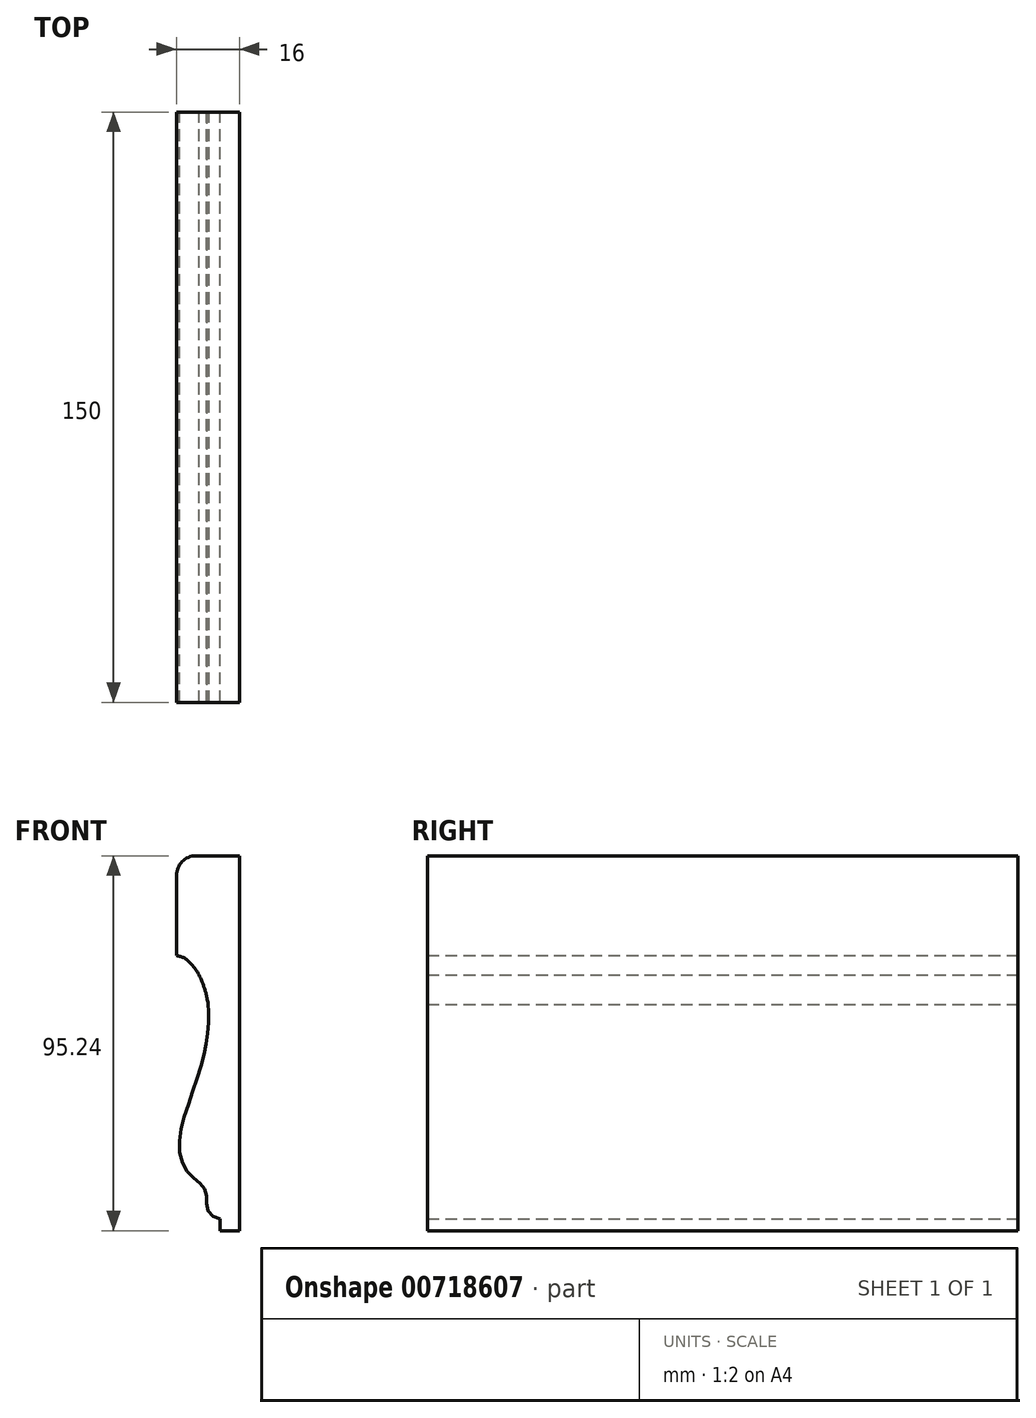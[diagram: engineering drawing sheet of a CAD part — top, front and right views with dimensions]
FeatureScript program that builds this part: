
annotation { "Feature Type Name" : "Feature", "Feature Type Description" : "" }
export const myFeature = defineFeature(function(context is Context, id is Id, definition is map)
    precondition{}
    {
        {
            var Q0;
            Q0=qCreatedBy(makeId("Front.planeOp"),FACE);
            var sketch = newSketch(context, id + "F0", { "sketchPlane" : qUnion([Q0])});
            skLineSegment(sketch, "E0", {"start": v(34.1, 83.58) * mm, "end": v(18.1, 83.58) * mm});
            skLineSegment(sketch, "E1", {"start": v(18.1, 83.58) * mm, "end": v(18.1, 58.24) * mm});
            skFitSpline(sketch, "E2", {"points": [v(26.17, 45.87) * mm, v(26.17, 39.83) * mm, v(24.86, 32.08) * mm, v(21.3, 20.93) * mm, v(18.84, 10.65) * mm, v(20.73, 3.48) * mm, v(24.5, 0) * mm, v(25.8, -2.94) * mm, v(26.17, -6.75) * mm, v(29.18, -8.66) * mm], "startDerivative": vector(6.37, -27.84) * mm, "endDerivative": vector(35.61, -4.93) * mm});
            skLineSegment(sketch, "E3", {"start": v(29.18, -8.66) * mm, "end": v(29.18, -11.66) * mm});
            skLineSegment(sketch, "E4", {"start": v(29.18, -11.66) * mm, "end": v(34.1, -11.66) * mm});
            skLineSegment(sketch, "E5", {"start": v(34.1, -11.66) * mm, "end": v(34.1, 83.58) * mm});
            skFitSpline(sketch, "E6", {"points": [v(23.83, 53.37) * mm, v(26.17, 45.87) * mm], "startDerivative": vector(4.05, -9.37) * mm, "endDerivative": vector(1.74, -9.99) * mm});
            skFitSpline(sketch, "E7", {"points": [v(18.1, 58.24) * mm, v(20.6, 57.3) * mm, v(23.83, 53.37) * mm], "startDerivative": vector(5.76, -1.24) * mm, "endDerivative": vector(4.47, -7.75) * mm});
            skSolve(sketch);
        }
        {
            var Q0;
            Q0=makeQuery(id+"F0.imprint","IMPRINT",FACE,{"disambiguationData":[TD([[makeQuery(id+"F0.imprint","IMPRINT",EDGE,{"derivedFrom":sQuery(id+"F0.wireOp",EDGE,"E0")}),1.0]])]});
            extrude(context, id + "F1", {"entities" : qUnion([Q0]), "depth" : 150 * mm, "offsetDistance" : 25 * mm});
        }
        {
            var Q0;
            Q0=makeQuery(id+"F1.opExtrude","SWEPT_EDGE",EDGE,{"disambiguationData":[OSD([sQuery(id+"F0.wireOp",EDGE,"E0"),sQuery(id+"F0.wireOp",EDGE,"E1")])]});
            fillet(context, id + "F2", {"entities" : qUnion([Q0]), "radius" : 5 * mm, "tangentPropagation" : true, "allowEdgeOverflow" : false});
        }
    });
